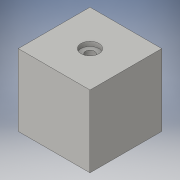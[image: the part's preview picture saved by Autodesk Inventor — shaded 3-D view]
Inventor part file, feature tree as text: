
AUTODESK INVENTOR PART (.ipt)
format: ipt  version: 2016 SP2 (Build 200236200, 236)  size: 93,184 bytes
history: native  units: in
note: dims shown in document units (in); Inventor stores cm internally (conversion verified against a paired STEP export)
features: sketch x2, extrude x1, hole x1
ambient origin geometry x8: Origin, YZ Plane, XZ Plane, XY Plane, X Axis, Y Axis, Z Axis, Center Point
bodies: Solid1 (feature_tree)
feature tree (4):
  extrude  "Extrusion1"  Depth=4.0in
  hole  "Hole1"  [1 undecoded]
  sketch  "Sketch1"  dims[d0=4.0in d1=4.0in]
  sketch  "Sketch2"  dims[d2=4.0in d3=0.0in d4=2.0in d5=0.5in d6=0.75in d7=1.0in d8=0.25in d9=0.5635in d10=3.0in d11=0.8108in]
note: 1 required parameter value undecoded (feature->parameter linkage not recoverable at this tier; creation-order binding heuristic only, values carry confidence <= 0.55)
